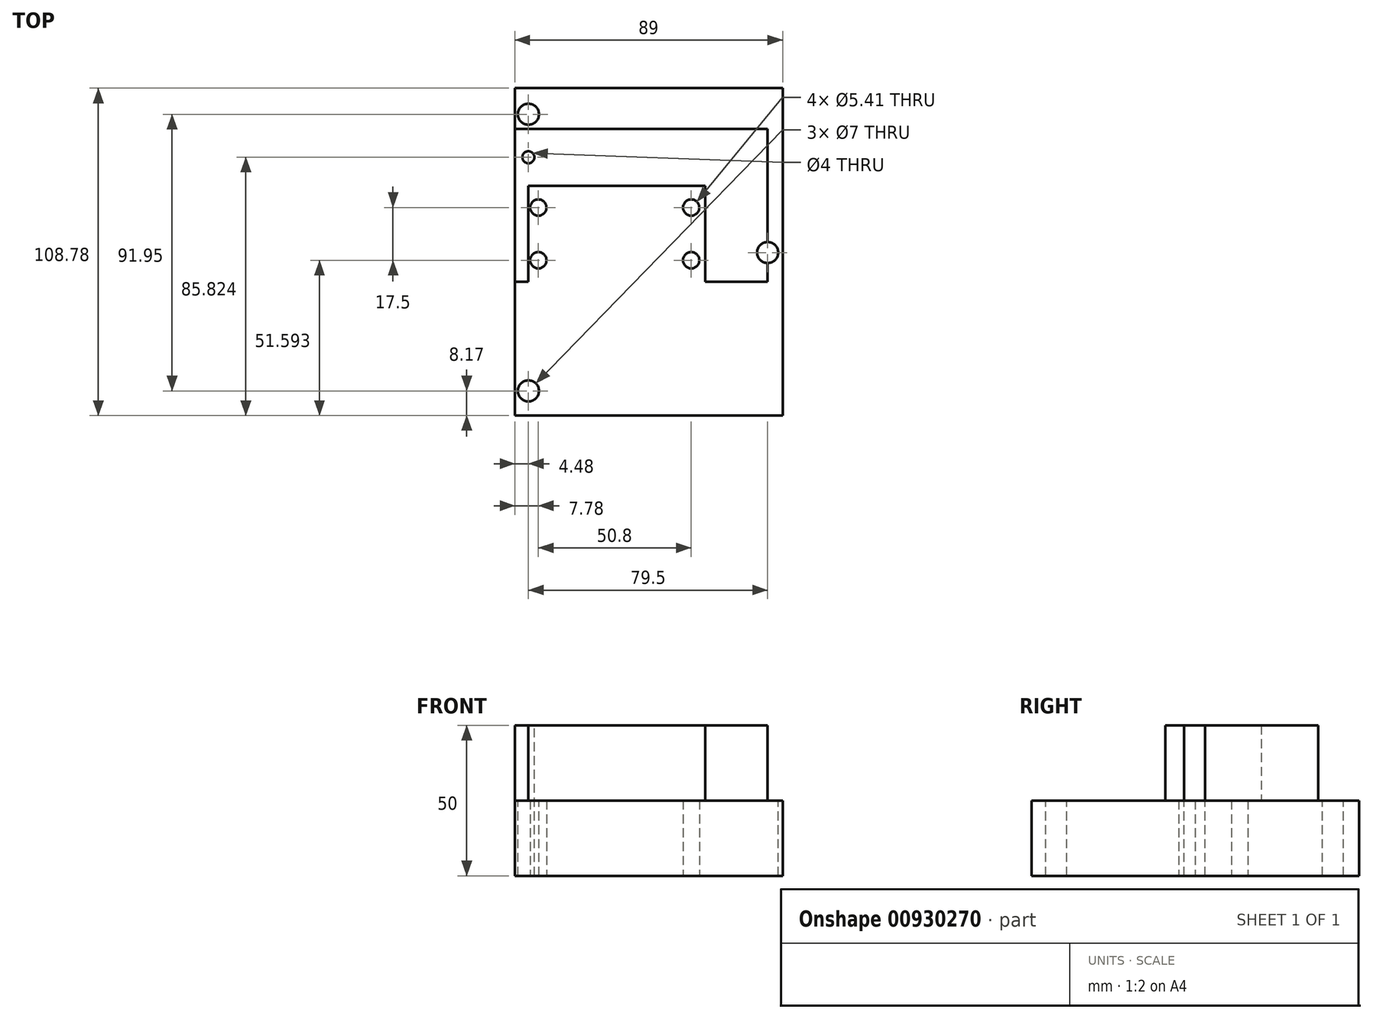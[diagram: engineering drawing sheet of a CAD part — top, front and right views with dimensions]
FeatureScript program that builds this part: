
annotation { "Feature Type Name" : "Feature", "Feature Type Description" : "" }
export const myFeature = defineFeature(function(context is Context, id is Id, definition is map)
    precondition{}
    {
        {
            var Q0;
            Q0=qCreatedBy(makeId("Top.planeOp"),FACE);
            var sketch = newSketch(context, id + "F0", { "sketchPlane" : qUnion([Q0])});
            skLineSegment(sketch, "E0.bottom", {"start": v(0, 0) * mm, "end": v(79.5, 0) * mm});
            skLineSegment(sketch, "E0.top", {"start": v(0, 91.95) * mm, "end": v(79.5, 91.95) * mm});
            skLineSegment(sketch, "E0.left", {"start": v(0, 0) * mm, "end": v(0, 91.95) * mm});
            skLineSegment(sketch, "E0.right", {"start": v(79.5, 0) * mm, "end": v(79.5, 91.95) * mm});
            skCircle(sketch, "E1", {"center": v(0, 91.95) * mm, "radius": 3.5 * mm});
            skCircle(sketch, "E2", {"center": v(0, 0) * mm, "radius": 3.5 * mm});
            skCircle(sketch, "E3", {"center": v(79.5, 45.98) * mm, "radius": 3.5 * mm});
            skLineSegment(sketch, "E4", {"start": v(-19.45, 106.17) * mm, "end": v(105.88, 106.17) * mm});
            skLineSegment(sketch, "E5.bottom", {"start": v(3.3, 43.42) * mm, "end": v(54.1, 43.42) * mm});
            skLineSegment(sketch, "E5.top", {"start": v(3.3, 60.92) * mm, "end": v(54.1, 60.92) * mm});
            skLineSegment(sketch, "E5.left", {"start": v(3.3, 43.42) * mm, "end": v(3.3, 60.92) * mm});
            skLineSegment(sketch, "E5.right", {"start": v(54.1, 43.42) * mm, "end": v(54.1, 60.92) * mm});
            skLineSegment(sketch, "E6", {"start": v(28.7, 113.86) * mm, "end": v(28.7, 96.45) * mm});
            skLineSegment(sketch, "E7.bottom", {"start": v(-4.48, 36.26) * mm, "end": v(84.52, 36.26) * mm});
            skLineSegment(sketch, "E7.top", {"start": v(-4.48, 87.06) * mm, "end": v(84.52, 87.06) * mm});
            skLineSegment(sketch, "E7.left", {"start": v(-4.48, 36.26) * mm, "end": v(-4.48, 87.06) * mm});
            skLineSegment(sketch, "E7.right", {"start": v(84.52, 36.26) * mm, "end": v(84.52, 87.06) * mm});
            skLineSegment(sketch, "E8.bottom", {"start": v(-1.3, 68.17) * mm, "end": v(58.7, 68.17) * mm});
            skLineSegment(sketch, "E8.top", {"start": v(-1.3, 36.17) * mm, "end": v(58.7, 36.17) * mm});
            skLineSegment(sketch, "E8.left", {"start": v(-1.3, 68.17) * mm, "end": v(-1.3, 36.17) * mm});
            skLineSegment(sketch, "E8.right", {"start": v(58.7, 68.17) * mm, "end": v(58.7, 36.17) * mm});
            skCircle(sketch, "E9", {"center": v(79.5, 45.98) * mm, "radius": 2.4 * mm});
            skLineSegment(sketch, "E10.bottom", {"start": v(-4.48, 100.61) * mm, "end": v(84.52, 100.61) * mm});
            skLineSegment(sketch, "E10.top", {"start": v(-4.48, -8.17) * mm, "end": v(84.52, -8.17) * mm});
            skLineSegment(sketch, "E10.left", {"start": v(-4.48, 100.61) * mm, "end": v(-4.48, -8.17) * mm});
            skLineSegment(sketch, "E10.right", {"start": v(84.52, 100.61) * mm, "end": v(84.52, -8.17) * mm});
            skCircle(sketch, "E11", {"center": v(0, 77.65) * mm, "radius": 2 * mm});
            skSolve(sketch);
        }
        {
            var Q0;
            {var subQ1=sQuery(id+"F0.wireOp",EDGE,"E0.right");var subQ4=sQuery(id+"F0.wireOp",EDGE,"E7.bottom");var subQ5=makeQuery(id+"F0.imprint","INTERSECT",VERTEX,{"derivedFrom":[subQ1,subQ4]});Q0=makeQuery(id+"F0.imprint","IMPRINT",FACE,{"disambiguationData":[TD([[makeQuery(id+"F0.imprint","IMPRINT",EDGE,{"disambiguationData":[TD([[subQ5,-1.0]])],"derivedFrom":subQ1}),-1.0]])]});}
            var Q1;
            {var subQ1=sQuery(id+"F0.wireOp",EDGE,"E0.top");var subQ10=sQuery(id+"F0.wireOp",EDGE,"E0.right");var subQ11=makeQuery(id+"F0.imprint","INTERSECT",VERTEX,{"derivedFrom":[subQ1,subQ10]});Q1=makeQuery(id+"F0.imprint","IMPRINT",FACE,{"disambiguationData":[TD([[makeQuery(id+"F0.imprint","IMPRINT",EDGE,{"disambiguationData":[TD([[subQ11,1.0]])],"derivedFrom":subQ1}),1.0]])]});}
            var Q2;
            {var subQ9=sQuery(id+"F0.wireOp",EDGE,"E10.top");Q2=makeQuery(id+"F0.imprint","IMPRINT",FACE,{"disambiguationData":[TD([[makeQuery(id+"F0.imprint","IMPRINT",EDGE,{"derivedFrom":subQ9}),1.0]])]});}
            var Q3;
            {var subQ0=sQuery(id+"F0.wireOp",EDGE,"E0.right");var subQ1=sQuery(id+"F0.wireOp",EDGE,"E0.top");var subQ2=makeQuery(id+"F0.imprint","INTERSECT",VERTEX,{"derivedFrom":[subQ1,subQ0]});Q3=makeQuery(id+"F0.imprint","IMPRINT",FACE,{"disambiguationData":[TD([[makeQuery(id+"F0.imprint","IMPRINT",EDGE,{"disambiguationData":[TD([[subQ2,1.0]])],"derivedFrom":subQ1}),-1.0]])]});}
            var Q4;
            Q4=makeQuery(id+"F0.imprint","IMPRINT",FACE,{"disambiguationData":[TD([[makeQuery(id+"F0.imprint","IMPRINT",EDGE,{"derivedFrom":sQuery(id+"F0.wireOp",EDGE,"E5.bottom")}),1.0]])]});
            var Q5;
            {var subQ6=sQuery(id+"F0.wireOp",EDGE,"E0.left");var subQ12=sQuery(id+"F0.wireOp",EDGE,"E8.bottom");var subQ13=makeQuery(id+"F0.imprint","INTERSECT",VERTEX,{"derivedFrom":[subQ6,subQ12]});Q5=makeQuery(id+"F0.imprint","IMPRINT",FACE,{"disambiguationData":[TD([[makeQuery(id+"F0.imprint","IMPRINT",EDGE,{"disambiguationData":[TD([[subQ13,-1.0]])],"derivedFrom":subQ6}),-1.0]])]});}
            var Q6;
            {var subQ3=sQuery(id+"F0.wireOp",EDGE,"E0.left");var subQ9=sQuery(id+"F0.wireOp",EDGE,"E8.bottom");var subQ10=makeQuery(id+"F0.imprint","INTERSECT",VERTEX,{"derivedFrom":[subQ3,subQ9]});Q6=makeQuery(id+"F0.imprint","IMPRINT",FACE,{"disambiguationData":[TD([[makeQuery(id+"F0.imprint","IMPRINT",EDGE,{"disambiguationData":[TD([[subQ10,-1.0]])],"derivedFrom":subQ3}),1.0]])]});}
            var Q7;
            {var subQ1=sQuery(id+"F0.wireOp",EDGE,"E0.bottom");var subQ6=sQuery(id+"F0.wireOp",EDGE,"E0.right");var subQ10=makeQuery(id+"F0.imprint","INTERSECT",VERTEX,{"derivedFrom":[subQ1,subQ6]});Q7=makeQuery(id+"F0.imprint","IMPRINT",FACE,{"disambiguationData":[TD([[makeQuery(id+"F0.imprint","IMPRINT",EDGE,{"disambiguationData":[TD([[subQ10,1.0]])],"derivedFrom":subQ1}),1.0]])]});}
            var Q8;
            Q8=makeQuery(id+"F0.imprint","IMPRINT",FACE,{"disambiguationData":[TD([[makeQuery(id+"F0.imprint","IMPRINT",EDGE,{"derivedFrom":sQuery(id+"F0.wireOp",EDGE,"E5.bottom")}),-1.0]])]});
            var Q9;
            {var subQ0=sQuery(id+"F0.wireOp",EDGE,"E7.bottom");var subQ1=sQuery(id+"F0.wireOp",EDGE,"E0.left");var subQ2=makeQuery(id+"F0.imprint","INTERSECT",VERTEX,{"derivedFrom":[subQ1,subQ0]});Q9=makeQuery(id+"F0.imprint","IMPRINT",FACE,{"disambiguationData":[TD([[makeQuery(id+"F0.imprint","IMPRINT",EDGE,{"disambiguationData":[TD([[subQ2,-1.0]])],"derivedFrom":subQ1}),1.0]])]});}
            var Q10;
            {var subQ0=sQuery(id+"F0.wireOp",EDGE,"E8.top");var subQ1=sQuery(id+"F0.wireOp",EDGE,"E0.left");var subQ2=makeQuery(id+"F0.imprint","INTERSECT",VERTEX,{"derivedFrom":[subQ1,subQ0]});Q10=makeQuery(id+"F0.imprint","IMPRINT",FACE,{"disambiguationData":[TD([[makeQuery(id+"F0.imprint","IMPRINT",EDGE,{"disambiguationData":[TD([[subQ2,-1.0]])],"derivedFrom":subQ1}),-1.0]])]});}
            var Q11;
            {var subQ0=sQuery(id+"F0.wireOp",EDGE,"E8.top");var subQ1=sQuery(id+"F0.wireOp",EDGE,"E0.left");var subQ2=makeQuery(id+"F0.imprint","INTERSECT",VERTEX,{"derivedFrom":[subQ1,subQ0]});Q11=makeQuery(id+"F0.imprint","IMPRINT",FACE,{"disambiguationData":[TD([[makeQuery(id+"F0.imprint","IMPRINT",EDGE,{"disambiguationData":[TD([[subQ2,-1.0]])],"derivedFrom":subQ1}),1.0]])]});}
            extrude(context, id + "F1", {"entities" : qUnion([Q0, Q1, Q2, Q3, Q4, Q5, Q6, Q7, Q8, Q9, Q10, Q11]), "oppositeDirection" : true, "depth" : 25 * mm, "offsetDistance" : 25 * mm});
        }
        {
            var Q0;
            Q0=sQuery(id+"F0.wireOp",VERTEX,"E5.top.start");
            var Q1;
            Q1=sQuery(id+"F0.wireOp",VERTEX,"E5.bottom.start");
            var Q2;
            Q2=sQuery(id+"F0.wireOp",VERTEX,"E5.bottom.end");
            var Q3;
            Q3=sQuery(id+"F0.wireOp",VERTEX,"E5.top.end");
            var Q4;
            Q4=makeQuery(id+"F1.opExtrude","SWEPT_BODY",BODY,{"disambiguationData":[OSD([sQuery(id+"F0.wireOp",EDGE,"E1"),sQuery(id+"F0.wireOp",EDGE,"E2"),sQuery(id+"F0.wireOp",EDGE,"E3"),sQuery(id+"F0.wireOp",EDGE,"E10.bottom"),sQuery(id+"F0.wireOp",EDGE,"E10.top"),sQuery(id+"F0.wireOp",EDGE,"E10.left"),sQuery(id+"F0.wireOp",EDGE,"E10.right"),sQuery(id+"F0.wireOp",EDGE,"E11")])]});
            hole(context, id + "F2", {"style" : HoleStyle.SIMPLE, "endStyle" : HoleEndStyle.THROUGH, "standardTappedOrClearance" : lookupTablePath({ "standard" : "ANSI", "engagement" : "75%", "pitch" : "28 tpi", "size" : "1/4", "type" : "Tapped" }), "standardBlindInLast" : lookupTablePath({ "standard" : "ANSI", "engagement" : "75%", "pitch" : "28 tpi", "size" : "1/4", "type" : "Tapped" }), "holeDiameter" : 5.4 * mm, "majorDiameter" : 6.35 * mm, "showTappedDepth" : true, "isTappedThrough" : true, "tappedDepth" : 12 * mm, "tapClearance" : 3, "startFromSketch" : true, "locations" : qUnion([Q0, Q1, Q2, Q3]), "scope" : qUnion([Q4])});
        }
        {
            var Q0;
            {var subQ3=sQuery(id+"F0.wireOp",EDGE,"E0.left");var subQ9=sQuery(id+"F0.wireOp",EDGE,"E8.bottom");var subQ10=makeQuery(id+"F0.imprint","INTERSECT",VERTEX,{"derivedFrom":[subQ3,subQ9]});Q0=makeQuery(id+"F0.imprint","IMPRINT",FACE,{"disambiguationData":[TD([[makeQuery(id+"F0.imprint","IMPRINT",EDGE,{"disambiguationData":[TD([[subQ10,-1.0]])],"derivedFrom":subQ3}),1.0]])]});}
            var Q1;
            {var subQ6=sQuery(id+"F0.wireOp",EDGE,"E0.left");var subQ12=sQuery(id+"F0.wireOp",EDGE,"E8.bottom");var subQ13=makeQuery(id+"F0.imprint","INTERSECT",VERTEX,{"derivedFrom":[subQ6,subQ12]});Q1=makeQuery(id+"F0.imprint","IMPRINT",FACE,{"disambiguationData":[TD([[makeQuery(id+"F0.imprint","IMPRINT",EDGE,{"disambiguationData":[TD([[subQ13,-1.0]])],"derivedFrom":subQ6}),-1.0]])]});}
            var Q2;
            {var subQ0=sQuery(id+"F0.wireOp",EDGE,"E7.bottom");var subQ1=sQuery(id+"F0.wireOp",EDGE,"E0.left");var subQ2=makeQuery(id+"F0.imprint","INTERSECT",VERTEX,{"derivedFrom":[subQ1,subQ0]});Q2=makeQuery(id+"F0.imprint","IMPRINT",FACE,{"disambiguationData":[TD([[makeQuery(id+"F0.imprint","IMPRINT",EDGE,{"disambiguationData":[TD([[subQ2,-1.0]])],"derivedFrom":subQ1}),1.0]])]});}
            extrude(context, id + "F3", {"entities" : qUnion([Q0, Q1, Q2]), "operationType" : NewBodyOperationType.ADD, "depth" : 25 * mm, "offsetDistance" : 25 * mm});
        }
    });
